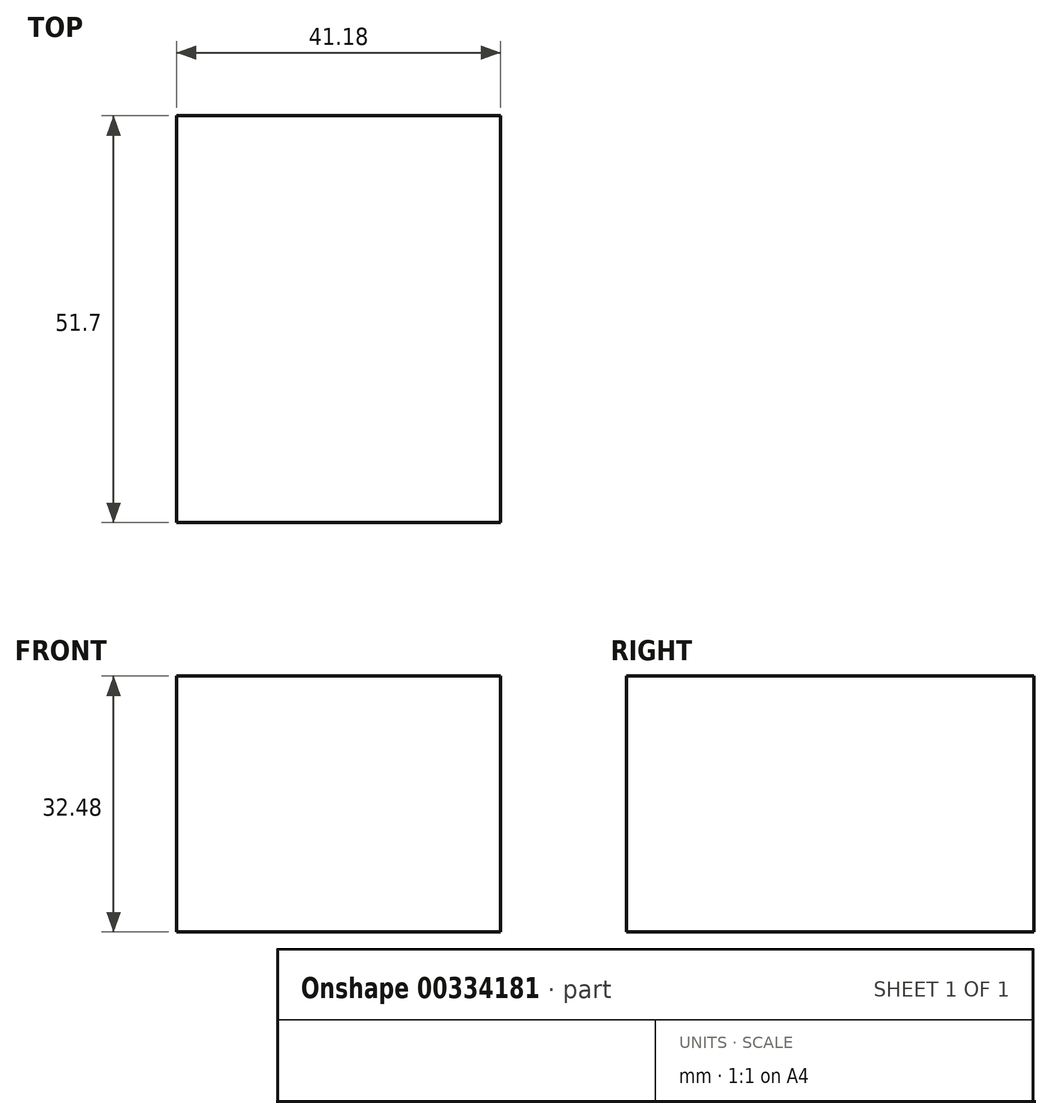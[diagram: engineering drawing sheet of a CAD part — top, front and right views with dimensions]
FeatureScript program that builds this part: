
annotation { "Feature Type Name" : "Feature", "Feature Type Description" : "" }
export const myFeature = defineFeature(function(context is Context, id is Id, definition is map)
    precondition{}
    {
        {
            var Q0;
            Q0=qCreatedBy(makeId("Front.planeOp"),FACE);
            var sketch = newSketch(context, id + "F0", { "sketchPlane" : qUnion([Q0])});
            skLineSegment(sketch, "E0.bottom", {"start": v(0, 0) * mm, "end": v(-41.18, 0) * mm});
            skLineSegment(sketch, "E0.top", {"start": v(0, 32.48) * mm, "end": v(-41.18, 32.48) * mm});
            skLineSegment(sketch, "E0.left", {"start": v(0, 0) * mm, "end": v(0, 32.48) * mm});
            skLineSegment(sketch, "E0.right", {"start": v(-41.18, 0) * mm, "end": v(-41.18, 32.48) * mm});
            skSolve(sketch);
        }
        {
            var Q0;
            Q0=makeQuery(id+"F0.imprint","IMPRINT",FACE,{"disambiguationData":[TD([[makeQuery(id+"F0.imprint","IMPRINT",EDGE,{"derivedFrom":sQuery(id+"F0.wireOp",EDGE,"E0.bottom")}),-1.0]])]});
            extrude(context, id + "F1", {"entities" : qUnion([Q0]), "depth" : 51.7 * mm});
        }
    });
